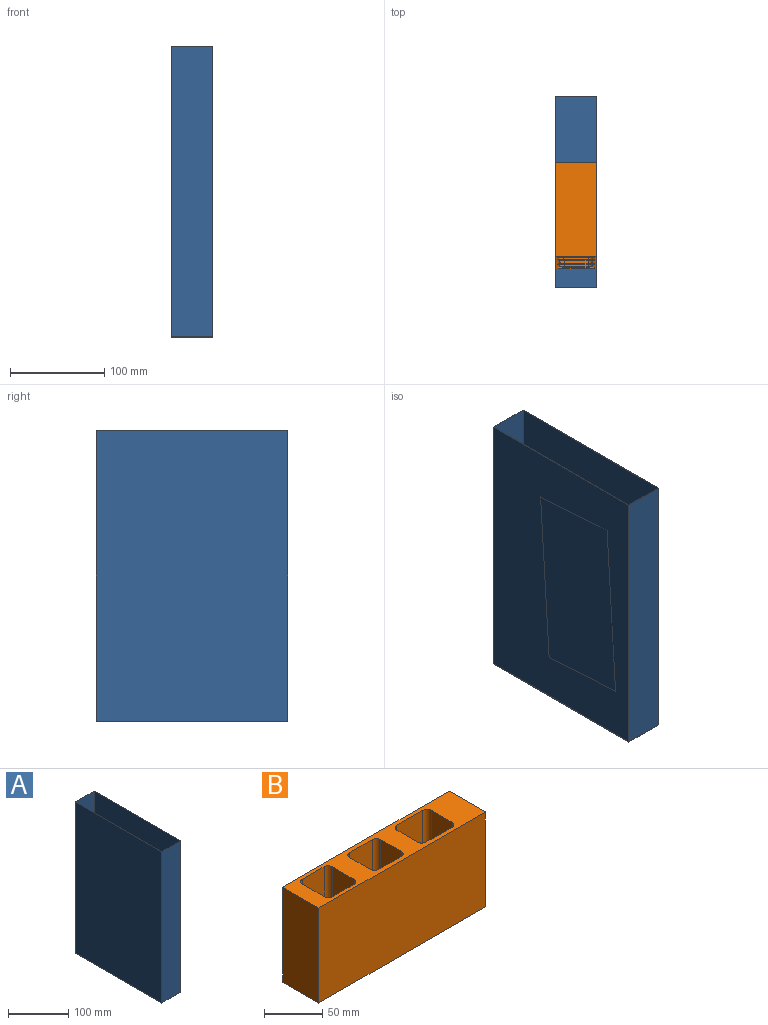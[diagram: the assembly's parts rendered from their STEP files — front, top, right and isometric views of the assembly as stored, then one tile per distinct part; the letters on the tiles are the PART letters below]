
ASSEMBLY  parts=2 mates=1
PART A: 11 faces, bbox 44.5x203.2x308 mm
  f0: plane 203.2x44.45mm, normal (0,0,1), area 123.6mm2, adj f1,f2,f3,f4,f6,f7,f8,f9
  f1: plane 307.95x44.45mm, normal (0,1,0), area 13688.4mm2, adj f0,f2,f4,f5
  f2: plane 307.95x203.2mm, normal (-1,0,0), area 62575.4mm2, adj f0,f1,f3,f5
  f3: plane 307.95x44.45mm, normal (0,-1,0), area 13688.4mm2, adj f0,f2,f4,f5
  f4: plane 307.95x203.2mm, normal (1,0,0), area 62575.4mm2, adj f0,f1,f3,f5
  f5: plane 203.2x44.45mm, normal (0,0,-1), area 9032.2mm2, adj f1,f2,f3,f4
  f6: plane 307.7x43.95mm, normal (0,-1,0), area 13523.4mm2, adj f0,f7,f9,f10
  f7: plane 307.7x202.7mm, normal (1,0,0), area 62370.8mm2, adj f0,f6,f8,f10
  f8: plane 307.7x43.95mm, normal (0,1,0), area 13523.4mm2, adj f0,f7,f9,f10
  f9: plane 307.7x202.7mm, normal (-1,0,0), area 62370.8mm2, adj f0,f6,f8,f10
  f10: plane 202.7x43.95mm, normal (0,0,1), area 8908.7mm2, adj f6,f7,f8,f9
PART B: 62 faces, bbox 202.9x44.2x100 mm
  f0: plane 202.9x44.15mm, normal (0,0,-1), area 2153.1mm2, adj f2,f3,f4,f5,f6,f7,f8,f9
  f1: plane 202.9x44.15mm, normal (0,0,1), area 4871.4mm2, adj f2,f3,f4,f5,f6,f7,f8,f9
  f2: plane 202.9x100mm, normal (0,1,0), area 20290mm2, adj f0,f1,f3,f5
  f3: plane 100x44.15mm, normal (-1,0,0), area 4415mm2, adj f0,f1,f2,f4
  f4: plane 202.9x100mm, normal (0,-1,0), area 20290mm2, adj f0,f1,f3,f5
  f5: plane 100x44.15mm, normal (1,0,0), area 4415mm2, adj f0,f1,f2,f4
  f6: plane 100x31.73mm, normal (0,-1,0), area 3173.3mm2, adj f0,f1,f7,f13
  f7: cylinder r=5mm len=100mm, axis (0,0,1), area 785.4mm2, adj f0,f1,f6,f8
  f8: plane 100x25.42mm, normal (1,0,0), area 2542.2mm2, adj f0,f1,f7,f9
  f9: cylinder r=5mm len=100mm, axis (0,0,1), area 785.4mm2, adj f0,f1,f8,f10
  f10: plane 100x31.73mm, normal (0,1,0), area 3173.3mm2, adj f0,f1,f9,f11
  f11: cylinder r=5mm len=100mm, axis (0,0,1), area 785.4mm2, adj f0,f1,f10,f12
  f12: plane 100x25.42mm, normal (-1,0,0), area 2542.2mm2, adj f0,f1,f11,f13
  f13: cylinder r=5mm len=100mm, axis (0,0,1), area 785.4mm2, adj f0,f1,f6,f12
  f14: plane 100x25.42mm, normal (-1,0,0), area 2542.2mm2, adj f0,f1,f15,f21
  f15: cylinder r=5mm len=100mm, axis (0,0,1), area 785.4mm2, adj f0,f1,f14,f16
  f16: plane 100x27.74mm, normal (0,-1,0), area 2774.3mm2, adj f0,f1,f15,f17
  f17: cylinder r=5mm len=100mm, axis (0,0,1), area 785.4mm2, adj f0,f1,f16,f18
  f18: plane 100x25.42mm, normal (1,0,0), area 2542.2mm2, adj f0,f1,f17,f19
  f19: cylinder r=5mm len=100mm, axis (0,0,1), area 785.4mm2, adj f0,f1,f18,f20
  f20: plane 100x27.74mm, normal (0,1,0), area 2774.3mm2, adj f0,f1,f19,f21
  f21: cylinder r=5mm len=100mm, axis (0,0,1), area 785.4mm2, adj f0,f1,f14,f20
  f22: plane 100x26.37mm, normal (0,-1,0), area 2636.8mm2, adj f0,f1,f23,f29
  f23: cylinder r=5mm len=100mm, axis (0,0,1), area 785.4mm2, adj f0,f1,f22,f24
  f24: plane 100x26.73mm, normal (1,0,0), area 2673.2mm2, adj f0,f1,f23,f25
  f25: cylinder r=5mm len=100mm, axis (0,0,1), area 785.4mm2, adj f0,f1,f24,f26
  f26: plane 100x26.37mm, normal (0,1,0), area 2636.8mm2, adj f0,f1,f25,f27
  f27: cylinder r=5mm len=100mm, axis (0,0,1), area 785.4mm2, adj f0,f1,f26,f28
  f28: plane 100x26.73mm, normal (-1,0,0), area 2673.2mm2, adj f0,f1,f27,f29
  f29: cylinder r=5mm len=100mm, axis (0,0,1), area 785.4mm2, adj f0,f1,f22,f28
  f30: cylinder r=7.5mm len=97.5mm, axis (0,0,1), area 845.4mm2, adj f0,f31,f34,f35
  f31: plane 97.5x25.42mm, normal (1,0,0), area 2478.6mm2, adj f0,f30,f32,f34
  f32: cylinder r=7.5mm len=97.5mm, axis (0,0,1), area 845.4mm2, adj f0,f31,f34,f36
  f33: plane 97.5x39.15mm, normal (-1,0,0), area 3817.1mm2, adj f0,f34,f35,f36
  f34: plane 39.15x30.78mm, normal (0,0,-1), area 1047mm2, adj f30,f31,f32,f33,f35,f36
  f35: plane 97.5x30.78mm, normal (0,-1,0), area 3001.3mm2, adj f0,f30,f33,f34
  f36: plane 97.5x30.78mm, normal (0,1,0), area 3001.3mm2, adj f0,f32,f33,f34
  f37: cylinder r=7.5mm len=97.5mm, axis (0,0,1), area 713.2mm2, adj f0,f38,f43,f44
  f38: plane 97.5x26.73mm, normal (1,0,0), area 2606.4mm2, adj f0,f37,f39,f43
  f39: cylinder r=7.5mm len=97.5mm, axis (0,0,1), area 713.2mm2, adj f0,f38,f43,f45
  f40: cylinder r=7.5mm len=97.5mm, axis (0,0,1), area 845.4mm2, adj f0,f41,f43,f45
  f41: plane 97.5x25.42mm, normal (-1,0,0), area 2478.6mm2, adj f0,f40,f42,f43
  f42: cylinder r=7.5mm len=97.5mm, axis (0,0,1), area 845.4mm2, adj f0,f41,f43,f44
  f43: plane 39.15x23.2mm, normal (0,0,-1), area 633.5mm2, adj f37,f38,f39,f40,f41,f42,f44,f45
  f44: plane 97.5x23.2mm, normal (0,-1,0), area 2262.4mm2, adj f0,f37,f42,f43
  f45: plane 97.5x23.2mm, normal (0,1,0), area 2262.4mm2, adj f0,f39,f40,f43
  f46: plane 97.5x23.83mm, normal (0,1,0), area 2323.9mm2, adj f0,f47,f51,f54
  f47: plane 39.15x23.83mm, normal (0,0,-1), area 616.9mm2, adj f46,f48,f49,f50,f51,f52,f53,f54
  f48: plane 97.5x23.83mm, normal (0,-1,0), area 2323.9mm2, adj f0,f47,f49,f53
  f49: cylinder r=7.5mm len=97.5mm, axis (0,0,1), area 845.4mm2, adj f0,f47,f48,f50
  f50: plane 97.5x25.42mm, normal (-1,0,0), area 2478.6mm2, adj f0,f47,f49,f51
  f51: cylinder r=7.5mm len=97.5mm, axis (0,0,1), area 845.4mm2, adj f0,f46,f47,f50
  f52: plane 97.5x25.42mm, normal (1,0,0), area 2478.6mm2, adj f0,f47,f53,f54
  f53: cylinder r=7.5mm len=97.5mm, axis (0,0,1), area 845.4mm2, adj f0,f47,f48,f52
  f54: cylinder r=7.5mm len=97.5mm, axis (0,0,1), area 845.4mm2, adj f0,f46,f47,f52
  f55: cylinder r=7.5mm len=97.5mm, axis (0,0,1), area 713.2mm2, adj f0,f56,f58,f60
  f56: plane 97.5x26.73mm, normal (-1,0,0), area 2606.4mm2, adj f0,f55,f57,f60
  f57: cylinder r=7.5mm len=97.5mm, axis (0,0,1), area 713.2mm2, adj f0,f56,f60,f61
  f58: plane 97.5x13.73mm, normal (0,1,0), area 1338.9mm2, adj f0,f55,f59,f60
  f59: plane 97.5x39.15mm, normal (1,0,0), area 3817.1mm2, adj f0,f58,f60,f61
  f60: plane 39.15x13.73mm, normal (0,0,-1), area 420.9mm2, adj f55,f56,f57,f58,f59,f61
  f61: plane 97.5x13.73mm, normal (0,-1,0), area 1338.9mm2, adj f0,f57,f59,f60
PLACE A t=(-1.24,-143.06,72.43)mm fixed
PLACE B rot(axis=(-0.59,0.59,0.55),122.1deg) t=(6.78,-125.49,-78.39)mm
MATE pin_slot B.f4 <-> A.f4  axis (1,0,0) through (28.85,-75.59,-81.55)mm
